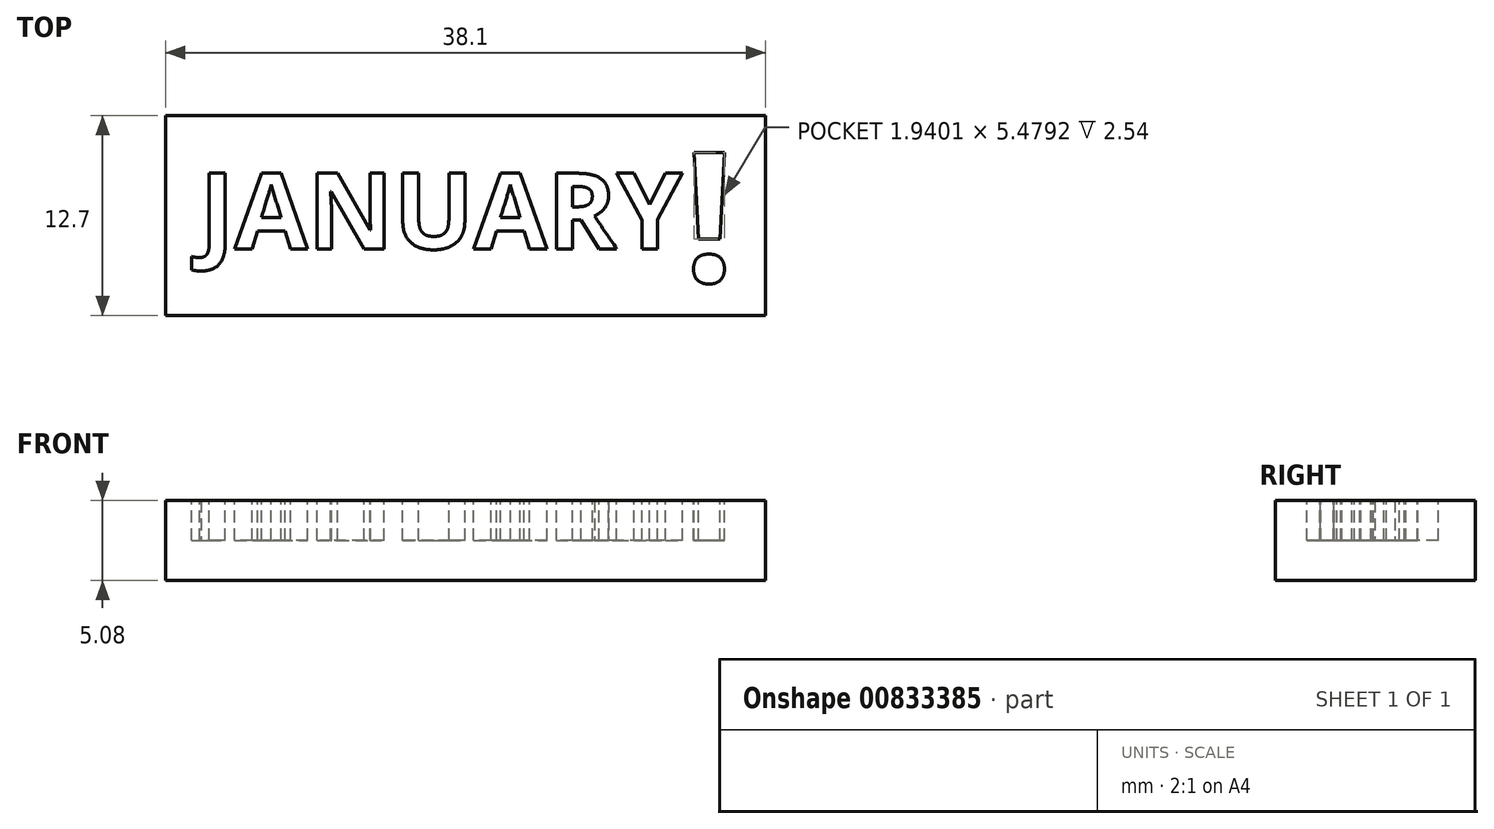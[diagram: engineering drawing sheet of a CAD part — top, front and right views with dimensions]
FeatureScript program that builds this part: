
annotation { "Feature Type Name" : "Feature", "Feature Type Description" : "" }
export const myFeature = defineFeature(function(context is Context, id is Id, definition is map)
    precondition{}
    {
        {
            var Q0;
            Q0=qCreatedBy(makeId("Top.planeOp"),FACE);
            var sketch = newSketch(context, id + "F0", { "sketchPlane" : qUnion([Q0])});
            skLineSegment(sketch, "E0.bottom", {"start": v(15.95, -21.38) * mm, "end": v(54.05, -21.38) * mm});
            skLineSegment(sketch, "E0.top", {"start": v(15.95, -34.08) * mm, "end": v(54.05, -34.08) * mm});
            skLineSegment(sketch, "E0.left", {"start": v(15.95, -21.38) * mm, "end": v(15.95, -34.08) * mm});
            skLineSegment(sketch, "E0.right", {"start": v(54.05, -21.38) * mm, "end": v(54.05, -34.08) * mm});
            skSolve(sketch);
        }
        {
            var Q0;
            Q0=makeQuery(id+"F0.imprint","IMPRINT",FACE,{"disambiguationData":[TD([[makeQuery(id+"F0.imprint","IMPRINT",EDGE,{"derivedFrom":sQuery(id+"F0.wireOp",EDGE,"E0.bottom")}),-1.0]])]});
            extrude(context, id + "F1", {"entities" : qUnion([Q0]), "depth" : 5.08 * mm, "offsetDistance" : 25.4 * mm});
        }
        {
            var Q0;
            Q0=makeQuery(id+"F1.opExtrude","CAP_FACE",FACE,{"disambiguationData":[OSD([sQuery(id+"F0.wireOp",EDGE,"E0.bottom"),sQuery(id+"F0.wireOp",EDGE,"E0.top"),sQuery(id+"F0.wireOp",EDGE,"E0.left"),sQuery(id+"F0.wireOp",EDGE,"E0.right")])],"isStart":false});
            var sketch = newSketch(context, id + "F2", { "sketchPlane" : qUnion([Q0])});
            skText(sketch, "E1", { "text": "JANUARY", "fontName": "OpenSans-Bold.ttf"});
            const initialGuessF2  = {"E1": [0.01811, -0.02985, 1, 0, 0.00484]};
            skSetInitialGuess(sketch, initialGuessF2);
            skSolve(sketch);
        }
        {
            var Q0;
            Q0 = qSketchRegion(id + "F2", true);
            extrude(context, id + "F3", {"entities" : qUnion([Q0]), "operationType" : NewBodyOperationType.REMOVE, "oppositeDirection" : true, "depth" : 2.54 * mm, "offsetDistance" : 25.4 * mm});
        }
        {
            var Q0;
            {var subQ0=sQuery(id+"F0.wireOp",EDGE,"E0.left");var subQ1=sQuery(id+"F0.wireOp",EDGE,"E0.bottom");var subQ2=sQuery(id+"F0.wireOp",EDGE,"E0.right");var subQ3=sQuery(id+"F0.wireOp",EDGE,"E0.top");Q0=makeQuery(id+"F3.boolean.opBoolean","SPLIT",FACE,{"disambiguationData":[TD([makeQuery(id+"F1.opExtrude","SWEPT_FACE",FACE,{"disambiguationData":[OSD([subQ1])]})])],"derivedFrom":makeQuery(id+"F1.opExtrude","CAP_FACE",FACE,{"disambiguationData":[OSD([subQ1,subQ3,subQ0,subQ2])],"isStart":false})});}
            var sketch = newSketch(context, id + "F4", { "sketchPlane" : qUnion([Q0])});
            skText(sketch, "E2", { "text": "!", "fontName": "OpenSans-Bold.ttf"});
            const initialGuessF4  = {"E2": [0.04882, -0.03194, 1, 0, 0.00827]};
            skSetInitialGuess(sketch, initialGuessF4);
            skSolve(sketch);
        }
        {
            var Q0;
            Q0 = qSketchRegion(id + "F4", true);
            extrude(context, id + "F5", {"entities" : qUnion([Q0]), "operationType" : NewBodyOperationType.REMOVE, "oppositeDirection" : true, "depth" : 2.54 * mm, "offsetDistance" : 25.4 * mm});
        }
    });
